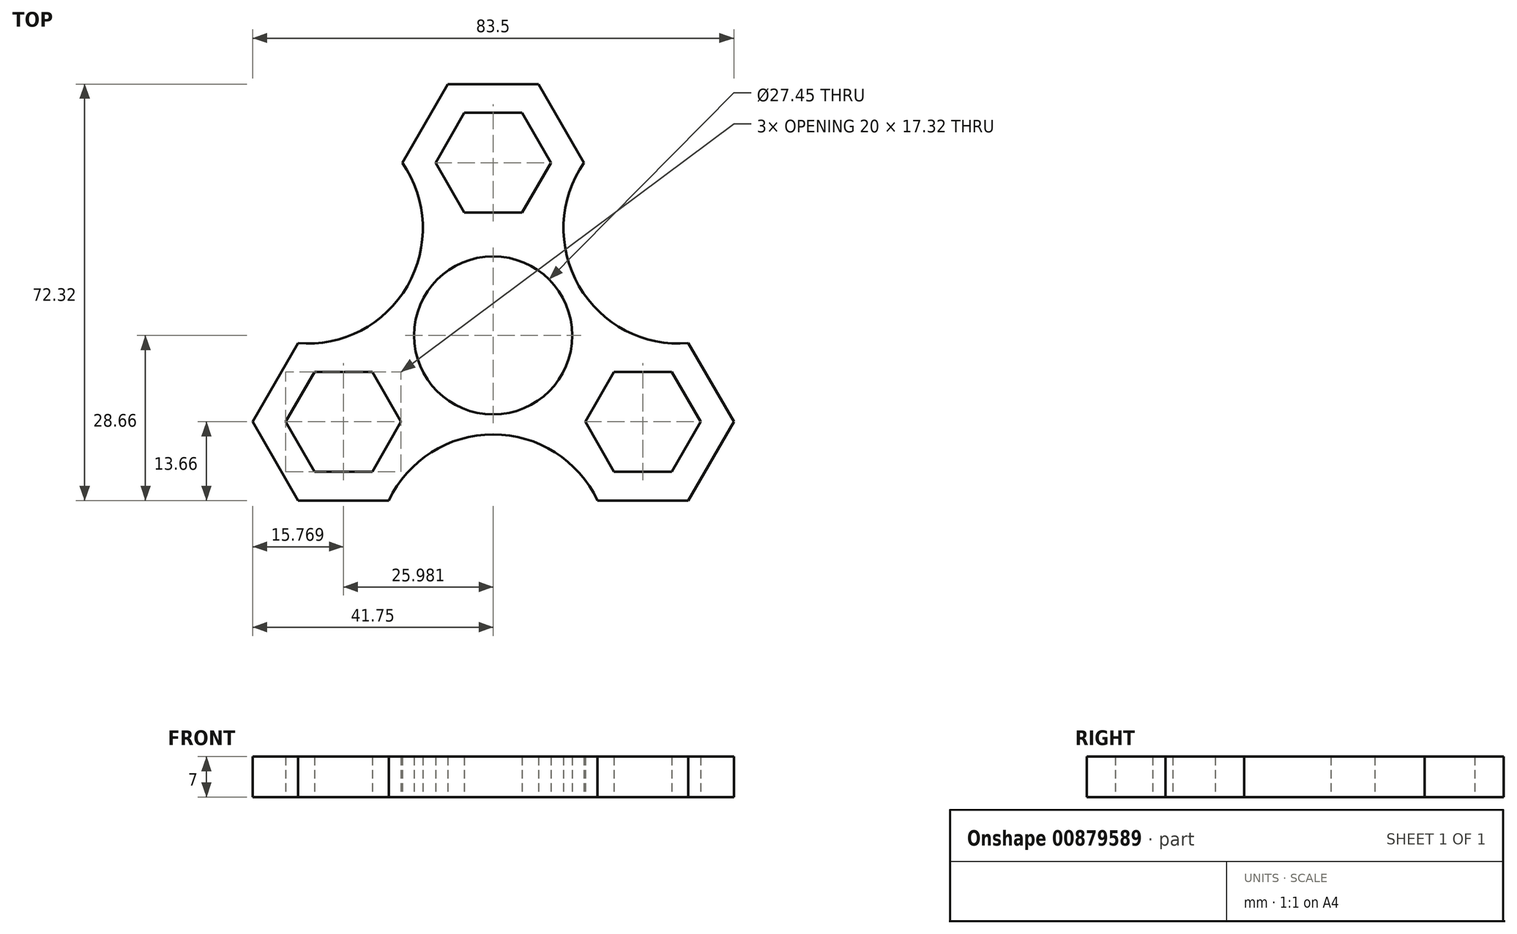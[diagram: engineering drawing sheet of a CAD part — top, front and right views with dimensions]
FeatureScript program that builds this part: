
annotation { "Feature Type Name" : "Feature", "Feature Type Description" : "" }
export const myFeature = defineFeature(function(context is Context, id is Id, definition is map)
    precondition{}
    {
        {
            var Q0;
            Q0=qCreatedBy(makeId("Top.planeOp"),FACE);
            var sketch = newSketch(context, id + "F0", { "sketchPlane" : qUnion([Q0])});
            skCircle(sketch, "E0", {"center": v(0, 0) * mm, "radius": 13.73 * mm});
            skCircle(sketch, "E1.cCircle", {"center": v(-25.98, -15) * mm, "radius": 8.66 * mm, "construction": true});
            skLineSegment(sketch, "E1.0", {"start": v(-20.98, -6.34) * mm, "end": v(-15.98, -15) * mm});
            skLineSegment(sketch, "E1.1", {"start": v(-15.98, -15) * mm, "end": v(-20.98, -23.66) * mm});
            skLineSegment(sketch, "E1.2", {"start": v(-20.98, -23.66) * mm, "end": v(-30.98, -23.66) * mm});
            skLineSegment(sketch, "E1.3", {"start": v(-30.98, -23.66) * mm, "end": v(-35.98, -15) * mm});
            skLineSegment(sketch, "E1.4", {"start": v(-35.98, -15) * mm, "end": v(-30.98, -6.34) * mm});
            skLineSegment(sketch, "E1.5", {"start": v(-30.98, -6.34) * mm, "end": v(-20.98, -6.34) * mm});
            skCircle(sketch, "E2.cCircle", {"center": v(25.98, -15) * mm, "radius": 8.66 * mm, "construction": true});
            skLineSegment(sketch, "E2.0", {"start": v(15.98, -15) * mm, "end": v(20.98, -6.34) * mm});
            skLineSegment(sketch, "E2.1", {"start": v(20.98, -6.34) * mm, "end": v(30.98, -6.34) * mm});
            skLineSegment(sketch, "E2.2", {"start": v(30.98, -6.34) * mm, "end": v(35.98, -15) * mm});
            skLineSegment(sketch, "E2.3", {"start": v(35.98, -15) * mm, "end": v(30.98, -23.66) * mm});
            skLineSegment(sketch, "E2.4", {"start": v(30.98, -23.66) * mm, "end": v(20.98, -23.66) * mm});
            skLineSegment(sketch, "E2.5", {"start": v(20.98, -23.66) * mm, "end": v(15.98, -15) * mm});
            skCircle(sketch, "E3.cCircle", {"center": v(0, 30) * mm, "radius": 8.66 * mm, "construction": true});
            skLineSegment(sketch, "E3.0", {"start": v(5, 21.34) * mm, "end": v(-5, 21.34) * mm});
            skLineSegment(sketch, "E3.1", {"start": v(-5, 21.34) * mm, "end": v(-10, 30) * mm});
            skLineSegment(sketch, "E3.2", {"start": v(-10, 30) * mm, "end": v(-5, 38.66) * mm});
            skLineSegment(sketch, "E3.3", {"start": v(-5, 38.66) * mm, "end": v(5, 38.66) * mm});
            skLineSegment(sketch, "E3.4", {"start": v(5, 38.66) * mm, "end": v(10, 30) * mm});
            skLineSegment(sketch, "E3.5", {"start": v(10, 30) * mm, "end": v(5, 21.34) * mm});
            skLineSegment(sketch, "E4.0", {"start": v(-5, 43.66) * mm, "end": v(5, 43.66) * mm});
            skLineSegment(sketch, "E5.0", {"start": v(-14.33, 32.5) * mm, "end": v(-9.33, 41.16) * mm});
            skLineSegment(sketch, "E6.0", {"start": v(9.33, 41.16) * mm, "end": v(14.33, 32.5) * mm});
            skLineSegment(sketch, "E7.0", {"start": v(-14.1, 27.11) * mm, "end": v(-14.33, 27.5) * mm});
            skLineSegment(sketch, "E8.0", {"start": v(14.33, 27.5) * mm, "end": v(14.1, 27.11) * mm});
            skLineSegment(sketch, "E9.0", {"start": v(-30.98, -1.34) * mm, "end": v(-30.53, -1.34) * mm});
            skLineSegment(sketch, "E10.0", {"start": v(-40.31, -12.5) * mm, "end": v(-35.31, -3.84) * mm});
            skLineSegment(sketch, "E11.0", {"start": v(-35.31, -26.16) * mm, "end": v(-40.31, -17.5) * mm});
            skLineSegment(sketch, "E12.0", {"start": v(-20.98, -28.66) * mm, "end": v(-30.98, -28.66) * mm});
            skLineSegment(sketch, "E13.0", {"start": v(-16.43, -25.77) * mm, "end": v(-16.65, -26.16) * mm});
            skLineSegment(sketch, "E14.0", {"start": v(16.65, -26.16) * mm, "end": v(16.43, -25.77) * mm});
            skLineSegment(sketch, "E15.0", {"start": v(30.98, -28.66) * mm, "end": v(20.98, -28.66) * mm});
            skLineSegment(sketch, "E16.0", {"start": v(40.3, -17.5) * mm, "end": v(35.31, -26.16) * mm});
            skLineSegment(sketch, "E17.0", {"start": v(35.31, -3.84) * mm, "end": v(40.31, -12.5) * mm});
            skLineSegment(sketch, "E18.0", {"start": v(30.53, -1.34) * mm, "end": v(30.98, -1.34) * mm});
            skLineSegment(sketch, "E19", {"start": v(14.33, 27.5) * mm, "end": v(15.77, 30) * mm});
            skLineSegment(sketch, "E20", {"start": v(14.33, 32.5) * mm, "end": v(15.77, 30) * mm});
            skLineSegment(sketch, "E21", {"start": v(-14.33, 27.5) * mm, "end": v(-15.77, 30) * mm});
            skLineSegment(sketch, "E22", {"start": v(-14.33, 32.5) * mm, "end": v(-15.77, 30) * mm});
            skLineSegment(sketch, "E23", {"start": v(-5, 43.66) * mm, "end": v(-7.89, 43.66) * mm});
            skLineSegment(sketch, "E24", {"start": v(5, 43.66) * mm, "end": v(7.89, 43.66) * mm});
            skLineSegment(sketch, "E25", {"start": v(-9.33, 41.16) * mm, "end": v(-7.89, 43.66) * mm});
            skLineSegment(sketch, "E26", {"start": v(9.33, 41.16) * mm, "end": v(7.89, 43.66) * mm});
            skLineSegment(sketch, "E27", {"start": v(30.98, -1.34) * mm, "end": v(33.87, -1.34) * mm});
            skLineSegment(sketch, "E28", {"start": v(35.31, -3.84) * mm, "end": v(33.87, -1.34) * mm});
            skLineSegment(sketch, "E29", {"start": v(40.31, -12.5) * mm, "end": v(41.75, -15) * mm});
            skLineSegment(sketch, "E30", {"start": v(40.3, -17.5) * mm, "end": v(41.75, -15) * mm});
            skLineSegment(sketch, "E31", {"start": v(35.31, -26.16) * mm, "end": v(33.87, -28.66) * mm});
            skLineSegment(sketch, "E32", {"start": v(16.65, -26.16) * mm, "end": v(18.1, -28.66) * mm});
            skLineSegment(sketch, "E33", {"start": v(30.98, -28.66) * mm, "end": v(33.87, -28.66) * mm});
            skLineSegment(sketch, "E34", {"start": v(20.98, -28.66) * mm, "end": v(18.1, -28.66) * mm});
            skLineSegment(sketch, "E35", {"start": v(-30.98, -1.34) * mm, "end": v(-33.87, -1.34) * mm});
            skLineSegment(sketch, "E36", {"start": v(-35.31, -3.84) * mm, "end": v(-33.87, -1.34) * mm});
            skLineSegment(sketch, "E37", {"start": v(-40.31, -12.5) * mm, "end": v(-41.75, -15) * mm});
            skLineSegment(sketch, "E38", {"start": v(-40.31, -17.5) * mm, "end": v(-41.75, -15) * mm});
            skLineSegment(sketch, "E39", {"start": v(-35.31, -26.16) * mm, "end": v(-33.87, -28.66) * mm});
            skLineSegment(sketch, "E40", {"start": v(-30.98, -28.66) * mm, "end": v(-33.87, -28.66) * mm});
            skLineSegment(sketch, "E41", {"start": v(-20.98, -28.66) * mm, "end": v(-18.1, -28.66) * mm});
            skLineSegment(sketch, "E42", {"start": v(-16.65, -26.16) * mm, "end": v(-18.1, -28.66) * mm});
            skArc(sketch, "E43", {"start": v(15.77, 30) * mm, "mid": v(14.88, 8.6) * mm, "end": v(33.87, -1.34) * mm});
            skArc(sketch, "E44", {"start": v(-33.87, -1.34) * mm, "mid": v(-14.88, 8.6) * mm, "end": v(-15.77, 30) * mm});
            skArc(sketch, "E45", {"start": v(18.1, -28.66) * mm, "mid": v(0, -17.18) * mm, "end": v(-18.1, -28.66) * mm});
            skSolve(sketch);
        }
        {
            var Q0;
            Q0=makeQuery(id+"F0.imprint","IMPRINT",FACE,{"disambiguationData":[TD([[makeQuery(id+"F0.imprint","IMPRINT",EDGE,{"derivedFrom":sQuery(id+"F0.wireOp",EDGE,"E0")}),-1.0]])]});
            extrude(context, id + "F1", {"entities" : qUnion([Q0]), "depth" : 7 * mm, "offsetDistance" : 25 * mm});
        }
    });
